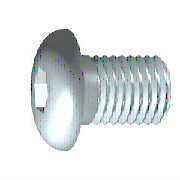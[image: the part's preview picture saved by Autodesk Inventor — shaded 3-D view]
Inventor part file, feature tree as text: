
AUTODESK INVENTOR PART (.ipt)
format: ipt  version: 2021 (Build 250183000, 183)  size: 205,312 bytes
history: native  units: mm (DEFAULTED — no unit token found)
features: sketch x2, extrude x1, plane x1
ambient origin geometry x7: Origin, YZ Plane, XY Plane, X Axis, Y Axis, Z Axis, Center Point
bodies: Solid1 (feature_tree), Body (feature_tree)
feature tree (4):
  extrude  "Slot"  Depth=0.306725mm
  plane  "Work Plane1"
  sketch  "Sketch1"  dims[d0=5.0mm d1=0.306725mm]
  sketch  "Sketch2"  dims[d2=1.65mm d3=1.04mm d4=60.0deg d5=3.0mm d6=3.0mm d7=2.309401mm d8=5.7mm d10=90.0deg d11=10.0mm d9=0.0mm d12=5.0mm d13=0.0mm d14=0.306725mm d15=0.306725mm d16=1.27mm d17=0.0mm d18=0.0mm d19=6.0mm d27=45.0deg d28=0.1mm d29=0.1mm]
